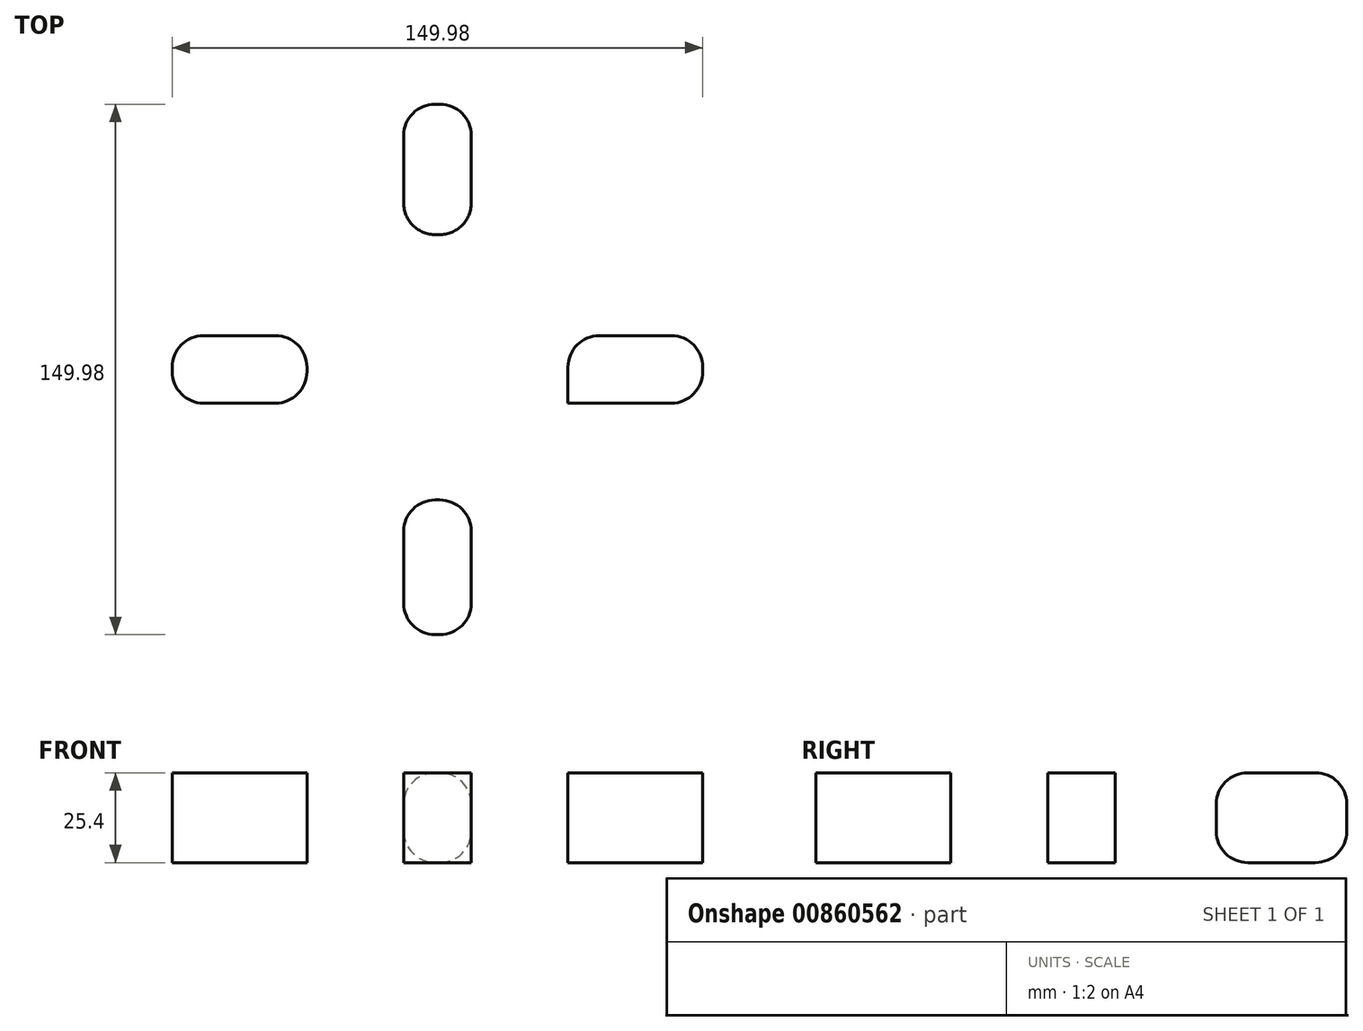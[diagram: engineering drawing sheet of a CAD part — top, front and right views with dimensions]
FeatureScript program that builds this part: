
annotation { "Feature Type Name" : "Feature", "Feature Type Description" : "" }
export const myFeature = defineFeature(function(context is Context, id is Id, definition is map)
    precondition{}
    {
        {
            var Q0;
            Q0=qCreatedBy(makeId("Top.planeOp"),FACE);
            var sketch = newSketch(context, id + "F0", { "sketchPlane" : qUnion([Q0])});
            skCircle(sketch, "E0", {"center": v(0, 0) * mm, "radius": 38.1 * mm});
            skLineSegment(sketch, "E1.bottom", {"start": v(9.53, 36.9) * mm, "end": v(-9.53, 36.9) * mm});
            skLineSegment(sketch, "E1.top", {"start": v(9.53, 75) * mm, "end": v(-9.53, 75) * mm});
            skLineSegment(sketch, "E1.left", {"start": v(9.53, 36.9) * mm, "end": v(9.53, 75) * mm});
            skLineSegment(sketch, "E1.right", {"start": v(-9.53, 36.9) * mm, "end": v(-9.53, 75) * mm});
            skLineSegment(sketch, "E2.1.1", {"start": v(9.52, 36.9) * mm, "end": v(9.52, 75) * mm});
            skLineSegment(sketch, "E2.1.3", {"start": v(9.52, 36.9) * mm, "end": v(-9.53, 36.9) * mm});
            skLineSegment(sketch, "E2.1.4", {"start": v(9.52, 75) * mm, "end": v(-9.53, 75) * mm});
            skLineSegment(sketch, "E2.2.1", {"start": v(9.52, 36.9) * mm, "end": v(9.52, 75) * mm});
            skLineSegment(sketch, "E2.2.3", {"start": v(9.52, 36.9) * mm, "end": v(-9.53, 36.9) * mm});
            skLineSegment(sketch, "E2.2.4", {"start": v(9.52, 75) * mm, "end": v(-9.53, 75) * mm});
            skLineSegment(sketch, "E2.3.1", {"start": v(9.52, 36.9) * mm, "end": v(9.52, 75) * mm});
            skLineSegment(sketch, "E2.3.3", {"start": v(9.52, 36.9) * mm, "end": v(-9.53, 36.9) * mm});
            skLineSegment(sketch, "E2.3.4", {"start": v(9.52, 75) * mm, "end": v(-9.53, 75) * mm});
            skLineSegment(sketch, "E2.4.1", {"start": v(9.52, 36.9) * mm, "end": v(9.52, 75) * mm});
            skLineSegment(sketch, "E2.4.3", {"start": v(9.52, 36.9) * mm, "end": v(-9.53, 36.9) * mm});
            skLineSegment(sketch, "E2.4.4", {"start": v(9.52, 75) * mm, "end": v(-9.53, 75) * mm});
            skLineSegment(sketch, "E2.anchor1", {"start": v(0, 0) * mm, "end": v(9.53, 36.9) * mm, "construction": true});
            skLineSegment(sketch, "E2.anchor2", {"start": v(0, 0) * mm, "end": v(9.52, 36.9) * mm, "construction": true});
            skLineSegment(sketch, "E3.1.0", {"start": v(-36.9, 9.52) * mm, "end": v(-75, 9.52) * mm});
            skLineSegment(sketch, "E3.1.1", {"start": v(-36.9, -9.53) * mm, "end": v(-75, -9.53) * mm});
            skLineSegment(sketch, "E3.1.2", {"start": v(-36.9, 9.52) * mm, "end": v(-36.9, -9.53) * mm});
            skLineSegment(sketch, "E3.1.3", {"start": v(-75, 9.52) * mm, "end": v(-75, -9.53) * mm});
            skLineSegment(sketch, "E3.2.0", {"start": v(-9.53, -36.9) * mm, "end": v(-9.52, -75) * mm});
            skLineSegment(sketch, "E3.2.1", {"start": v(9.53, -36.9) * mm, "end": v(9.53, -75) * mm});
            skLineSegment(sketch, "E3.2.2", {"start": v(-9.52, -36.9) * mm, "end": v(9.53, -36.9) * mm});
            skLineSegment(sketch, "E3.2.3", {"start": v(-9.52, -75) * mm, "end": v(9.53, -75) * mm});
            skLineSegment(sketch, "E3.3.0", {"start": v(36.9, -9.53) * mm, "end": v(75, -9.53) * mm});
            skLineSegment(sketch, "E3.3.1", {"start": v(36.9, 9.53) * mm, "end": v(75, 9.53) * mm});
            skLineSegment(sketch, "E3.3.2", {"start": v(36.9, -9.52) * mm, "end": v(36.9, 9.52) * mm});
            skLineSegment(sketch, "E3.3.3", {"start": v(75, -9.52) * mm, "end": v(75, 9.53) * mm});
            skSolve(sketch);
        }
        {
            var Q0;
            {var subQ4=sQuery(id+"F0.wireOp",EDGE,"E2.4.3");Q0=makeQuery(id+"F0.imprint","IMPRINT",FACE,{"disambiguationData":[TD([[makeQuery(id+"F0.imprint","IMPRINT",EDGE,{"derivedFrom":subQ4}),1.0]])]});}
            var Q1;
            {var subQ1=sQuery(id+"F0.wireOp",EDGE,"E3.1.0");Q1=makeQuery(id+"F0.imprint","IMPRINT",FACE,{"disambiguationData":[TD([[makeQuery(id+"F0.imprint","IMPRINT",EDGE,{"derivedFrom":subQ1}),1.0]])]});}
            var Q2;
            {var subQ0=sQuery(id+"F0.wireOp",EDGE,"E2.4.3");Q2=makeQuery(id+"F0.imprint","IMPRINT",FACE,{"disambiguationData":[TD([[makeQuery(id+"F0.imprint","IMPRINT",EDGE,{"derivedFrom":subQ0}),-1.0]])]});}
            var Q3;
            {var subQ1=sQuery(id+"F0.wireOp",EDGE,"E2.4.1");Q3=makeQuery(id+"F0.imprint","IMPRINT",FACE,{"disambiguationData":[TD([[makeQuery(id+"F0.imprint","IMPRINT",EDGE,{"derivedFrom":subQ1}),1.0]])]});}
            var Q4;
            {var subQ0=sQuery(id+"F0.wireOp",EDGE,"E3.1.2");Q4=makeQuery(id+"F0.imprint","IMPRINT",FACE,{"disambiguationData":[TD([[makeQuery(id+"F0.imprint","IMPRINT",EDGE,{"derivedFrom":subQ0}),-1.0]])]});}
            var Q5;
            {var subQ0=sQuery(id+"F0.wireOp",EDGE,"E3.2.2");Q5=makeQuery(id+"F0.imprint","IMPRINT",FACE,{"disambiguationData":[TD([[makeQuery(id+"F0.imprint","IMPRINT",EDGE,{"derivedFrom":subQ0}),-1.0]])]});}
            var Q6;
            {var subQ0=sQuery(id+"F0.wireOp",EDGE,"E3.3.2");Q6=makeQuery(id+"F0.imprint","IMPRINT",FACE,{"disambiguationData":[TD([[makeQuery(id+"F0.imprint","IMPRINT",EDGE,{"derivedFrom":subQ0}),-1.0]])]});}
            var Q7;
            {var subQ1=sQuery(id+"F0.wireOp",EDGE,"E3.3.0");Q7=makeQuery(id+"F0.imprint","IMPRINT",FACE,{"disambiguationData":[TD([[makeQuery(id+"F0.imprint","IMPRINT",EDGE,{"derivedFrom":subQ1}),1.0]])]});}
            var Q8;
            {var subQ1=sQuery(id+"F0.wireOp",EDGE,"E3.2.0");Q8=makeQuery(id+"F0.imprint","IMPRINT",FACE,{"disambiguationData":[TD([[makeQuery(id+"F0.imprint","IMPRINT",EDGE,{"derivedFrom":subQ1}),1.0]])]});}
            extrude(context, id + "F1", {"entities" : qUnion([Q0, Q1, Q2, Q3, Q4, Q5, Q6, Q7, Q8]), "depth" : 25.4 * mm, "offsetDistance" : 25.4 * mm});
        }
        {
            var Q0;
            Q0=makeQuery(id+"F1.opExtrude","CAP_FACE",FACE,{"disambiguationData":[OSD([sQuery(id+"F0.wireOp",EDGE,"E0"),sQuery(id+"F0.wireOp",EDGE,"E2.4.1"),sQuery(id+"F0.wireOp",EDGE,"E1.right"),sQuery(id+"F0.wireOp",EDGE,"E2.4.4"),sQuery(id+"F0.wireOp",EDGE,"E3.1.0"),sQuery(id+"F0.wireOp",EDGE,"E3.1.1"),sQuery(id+"F0.wireOp",EDGE,"E3.1.3"),sQuery(id+"F0.wireOp",EDGE,"E3.2.0"),sQuery(id+"F0.wireOp",EDGE,"E3.2.1"),sQuery(id+"F0.wireOp",EDGE,"E3.2.3"),sQuery(id+"F0.wireOp",EDGE,"E3.3.0"),sQuery(id+"F0.wireOp",EDGE,"E3.3.1"),sQuery(id+"F0.wireOp",EDGE,"E3.3.3")])],"isStart":false});
            var Q1;
            Q1=makeQuery(id+"F1.opExtrude","CAP_FACE",FACE,{"disambiguationData":[OSD([sQuery(id+"F0.wireOp",EDGE,"E0"),sQuery(id+"F0.wireOp",EDGE,"E2.4.1"),sQuery(id+"F0.wireOp",EDGE,"E1.right"),sQuery(id+"F0.wireOp",EDGE,"E2.4.4"),sQuery(id+"F0.wireOp",EDGE,"E3.1.0"),sQuery(id+"F0.wireOp",EDGE,"E3.1.1"),sQuery(id+"F0.wireOp",EDGE,"E3.1.3"),sQuery(id+"F0.wireOp",EDGE,"E3.2.0"),sQuery(id+"F0.wireOp",EDGE,"E3.2.1"),sQuery(id+"F0.wireOp",EDGE,"E3.2.3"),sQuery(id+"F0.wireOp",EDGE,"E3.3.0"),sQuery(id+"F0.wireOp",EDGE,"E3.3.1"),sQuery(id+"F0.wireOp",EDGE,"E3.3.3")])],"isStart":true});
            var Q2;
            Q2=makeQuery(id+"F1.opExtrude","SWEPT_EDGE",EDGE,{"disambiguationData":[OSD([sQuery(id+"F0.wireOp",EDGE,"E3.1.1"),sQuery(id+"F0.wireOp",EDGE,"E3.1.3")])]});
            var Q3;
            Q3=makeQuery(id+"F1.opExtrude","SWEPT_EDGE",EDGE,{"disambiguationData":[OSD([sQuery(id+"F0.wireOp",EDGE,"E3.2.0"),sQuery(id+"F0.wireOp",EDGE,"E3.2.3")])]});
            var Q4;
            Q4=makeQuery(id+"F1.opExtrude","SWEPT_EDGE",EDGE,{"disambiguationData":[OSD([sQuery(id+"F0.wireOp",EDGE,"E3.1.0"),sQuery(id+"F0.wireOp",EDGE,"E3.1.3")])]});
            var Q5;
            Q5=makeQuery(id+"F1.opExtrude","SWEPT_EDGE",EDGE,{"disambiguationData":[OSD([sQuery(id+"F0.wireOp",EDGE,"E1.right"),sQuery(id+"F0.wireOp",EDGE,"E2.4.4")])]});
            var Q6;
            Q6=makeQuery(id+"F1.opExtrude","SWEPT_EDGE",EDGE,{"disambiguationData":[OSD([sQuery(id+"F0.wireOp",EDGE,"E2.4.1"),sQuery(id+"F0.wireOp",EDGE,"E2.4.4")])]});
            var Q7;
            Q7=makeQuery(id+"F1.opExtrude","SWEPT_EDGE",EDGE,{"disambiguationData":[OSD([sQuery(id+"F0.wireOp",EDGE,"E3.3.1"),sQuery(id+"F0.wireOp",EDGE,"E3.3.3")])]});
            var Q8;
            Q8=makeQuery(id+"F1.opExtrude","SWEPT_EDGE",EDGE,{"disambiguationData":[OSD([sQuery(id+"F0.wireOp",EDGE,"E3.3.0"),sQuery(id+"F0.wireOp",EDGE,"E3.3.3")])]});
            var Q9;
            Q9=makeQuery(id+"F1.opExtrude","SWEPT_EDGE",EDGE,{"disambiguationData":[OSD([sQuery(id+"F0.wireOp",EDGE,"E3.2.1"),sQuery(id+"F0.wireOp",EDGE,"E3.2.3")])]});
            var Q10;
            Q10=makeQuery(id+"F1.opExtrude","SWEPT_EDGE",EDGE,{"disambiguationData":[OSD([sQuery(id+"F0.wireOp",EDGE,"E0"),sQuery(id+"F0.wireOp",EDGE,"E1.right"),sQuery(id+"F0.wireOp",EDGE,"E2.4.3")])]});
            var Q11;
            Q11=makeQuery(id+"F1.opExtrude","SWEPT_EDGE",EDGE,{"disambiguationData":[OSD([sQuery(id+"F0.wireOp",EDGE,"E0"),sQuery(id+"F0.wireOp",EDGE,"E3.1.0"),sQuery(id+"F0.wireOp",EDGE,"E3.1.2")])]});
            var Q12;
            Q12=makeQuery(id+"F1.opExtrude","SWEPT_EDGE",EDGE,{"disambiguationData":[OSD([sQuery(id+"F0.wireOp",EDGE,"E0"),sQuery(id+"F0.wireOp",EDGE,"E2.4.1"),sQuery(id+"F0.wireOp",EDGE,"E2.4.3")])]});
            var Q13;
            Q13=makeQuery(id+"F1.opExtrude","SWEPT_EDGE",EDGE,{"disambiguationData":[OSD([sQuery(id+"F0.wireOp",EDGE,"E0"),sQuery(id+"F0.wireOp",EDGE,"E3.3.1"),sQuery(id+"F0.wireOp",EDGE,"E3.3.2")])]});
            var Q14;
            Q14=makeQuery(id+"F1.opExtrude","SWEPT_EDGE",EDGE,{"disambiguationData":[OSD([sQuery(id+"F0.wireOp",EDGE,"E0"),sQuery(id+"F0.wireOp",EDGE,"E3.2.1"),sQuery(id+"F0.wireOp",EDGE,"E3.2.2")])]});
            var Q15;
            Q15=makeQuery(id+"F1.opExtrude","SWEPT_EDGE",EDGE,{"disambiguationData":[OSD([sQuery(id+"F0.wireOp",EDGE,"E0"),sQuery(id+"F0.wireOp",EDGE,"E3.2.0"),sQuery(id+"F0.wireOp",EDGE,"E3.2.2")])]});
            var Q16;
            Q16=makeQuery(id+"F1.opExtrude","SWEPT_EDGE",EDGE,{"disambiguationData":[OSD([sQuery(id+"F0.wireOp",EDGE,"E0"),sQuery(id+"F0.wireOp",EDGE,"E3.1.1"),sQuery(id+"F0.wireOp",EDGE,"E3.1.2")])]});
            fillet(context, id + "F2", {"entities" : qUnion([Q0, Q1, Q2, Q3, Q4, Q5, Q6, Q7, Q8, Q9, Q10, Q11, Q12, Q13, Q14, Q15, Q16]), "radius" : 8.9 * mm, "tangentPropagation" : true, "allowEdgeOverflow" : false});
        }
    });
